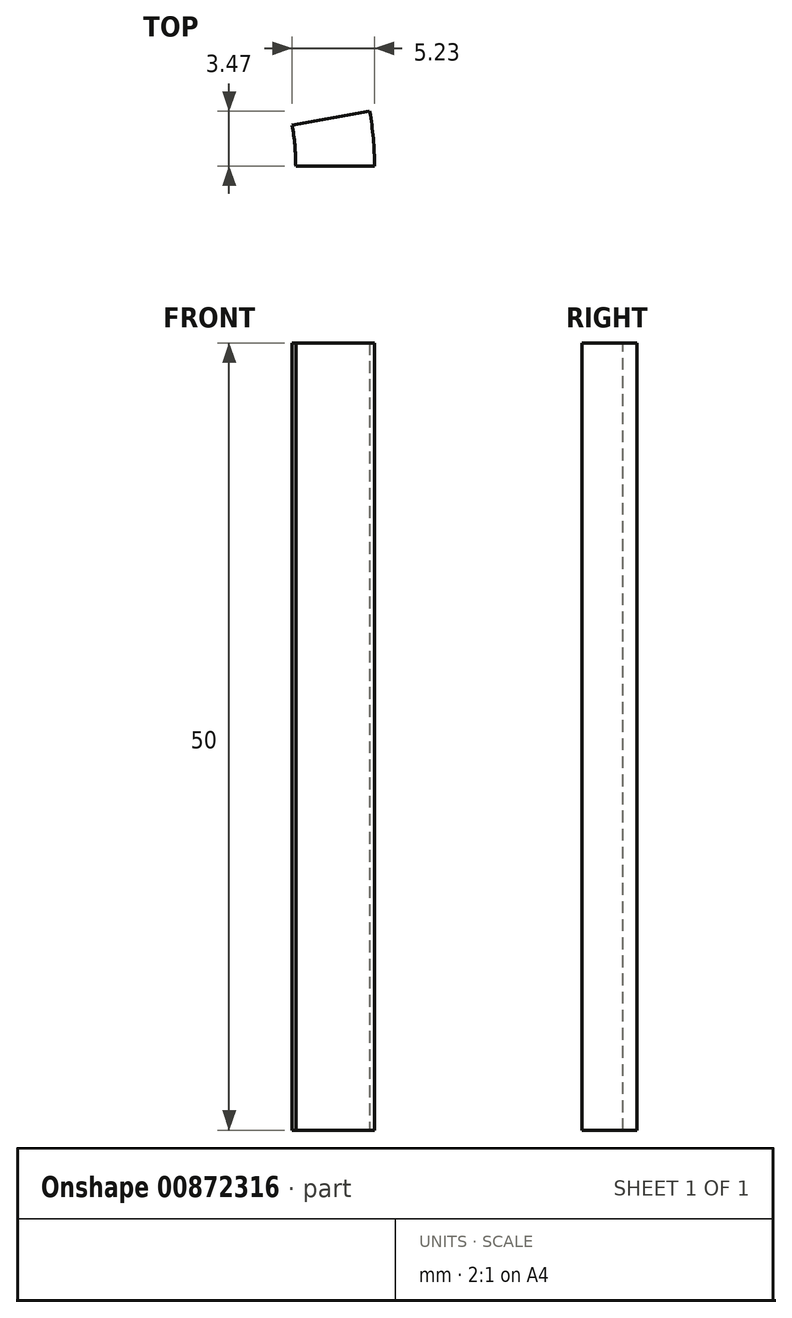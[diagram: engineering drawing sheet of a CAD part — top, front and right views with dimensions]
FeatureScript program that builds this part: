
annotation { "Feature Type Name" : "Feature", "Feature Type Description" : "" }
export const myFeature = defineFeature(function(context is Context, id is Id, definition is map)
    precondition{}
    {
        {
            var Q0;
            Q0=qCreatedBy(makeId("Front.planeOp"),FACE);
            var sketch = newSketch(context, id + "F0", { "sketchPlane" : qUnion([Q0])});
            skLineSegment(sketch, "E0", {"start": v(15, 0) * mm, "end": v(15, 10) * mm});
            skLineSegment(sketch, "E1", {"start": v(15, 10) * mm, "end": v(15, 20) * mm});
            skLineSegment(sketch, "E2", {"start": v(15, 20) * mm, "end": v(15, 30) * mm});
            skLineSegment(sketch, "E3", {"start": v(15, 30) * mm, "end": v(15, 40) * mm});
            skLineSegment(sketch, "E4", {"start": v(15, 40) * mm, "end": v(15, 50) * mm});
            skLineSegment(sketch, "E5", {"start": v(15, 50) * mm, "end": v(20, 50) * mm});
            skLineSegment(sketch, "E6", {"start": v(20, 50) * mm, "end": v(20, 0) * mm});
            skLineSegment(sketch, "E7", {"start": v(20, 0) * mm, "end": v(15, 0) * mm});
            skLineSegment(sketch, "E8", {"start": v(0, 0) * mm, "end": v(0, 50) * mm, "construction": true});
            skLineSegment(sketch, "E9", {"start": v(15, 10) * mm, "end": v(20, 10) * mm});
            skLineSegment(sketch, "E10", {"start": v(15, 20) * mm, "end": v(20, 20) * mm});
            skLineSegment(sketch, "E11", {"start": v(15, 30) * mm, "end": v(20, 30) * mm});
            skLineSegment(sketch, "E12", {"start": v(20, 30) * mm, "end": v(20, 40) * mm});
            skLineSegment(sketch, "E13", {"start": v(15, 40) * mm, "end": v(20, 40) * mm});
            skSolve(sketch);
        }
        {
            var Q0;
            Q0=makeQuery(id+"F0.imprint","IMPRINT",FACE,{"disambiguationData":[TD([[makeQuery(id+"F0.imprint","IMPRINT",EDGE,{"derivedFrom":sQuery(id+"F0.wireOp",EDGE,"E0")}),-1.0]])]});
            var Q1;
            Q1=makeQuery(id+"F0.imprint","IMPRINT",FACE,{"disambiguationData":[TD([[makeQuery(id+"F0.imprint","IMPRINT",EDGE,{"derivedFrom":sQuery(id+"F0.wireOp",EDGE,"E1")}),-1.0]])]});
            var Q2;
            Q2=makeQuery(id+"F0.imprint","IMPRINT",FACE,{"disambiguationData":[TD([[makeQuery(id+"F0.imprint","IMPRINT",EDGE,{"derivedFrom":sQuery(id+"F0.wireOp",EDGE,"E2")}),-1.0]])]});
            var Q3;
            Q3=makeQuery(id+"F0.imprint","IMPRINT",FACE,{"disambiguationData":[TD([[makeQuery(id+"F0.imprint","IMPRINT",EDGE,{"derivedFrom":sQuery(id+"F0.wireOp",EDGE,"E3")}),-1.0]])]});
            var Q4;
            Q4=makeQuery(id+"F0.imprint","IMPRINT",FACE,{"disambiguationData":[TD([[makeQuery(id+"F0.imprint","IMPRINT",EDGE,{"derivedFrom":sQuery(id+"F0.wireOp",EDGE,"E4")}),-1.0]])]});
            var Q5;
            Q5=sQuery(id+"F0.wireOp",EDGE,"E8");
            revolve(context, id + "F1", {"surfaceOperationType" : NewSurfaceOperationType.NEW, "entities" : qUnion([Q0, Q1, Q2, Q3, Q4]), "axis" : qUnion([Q5]), "revolveType" : RevolveType.ONE_DIRECTION, "angle" : 10 * degree});
        }
    });
